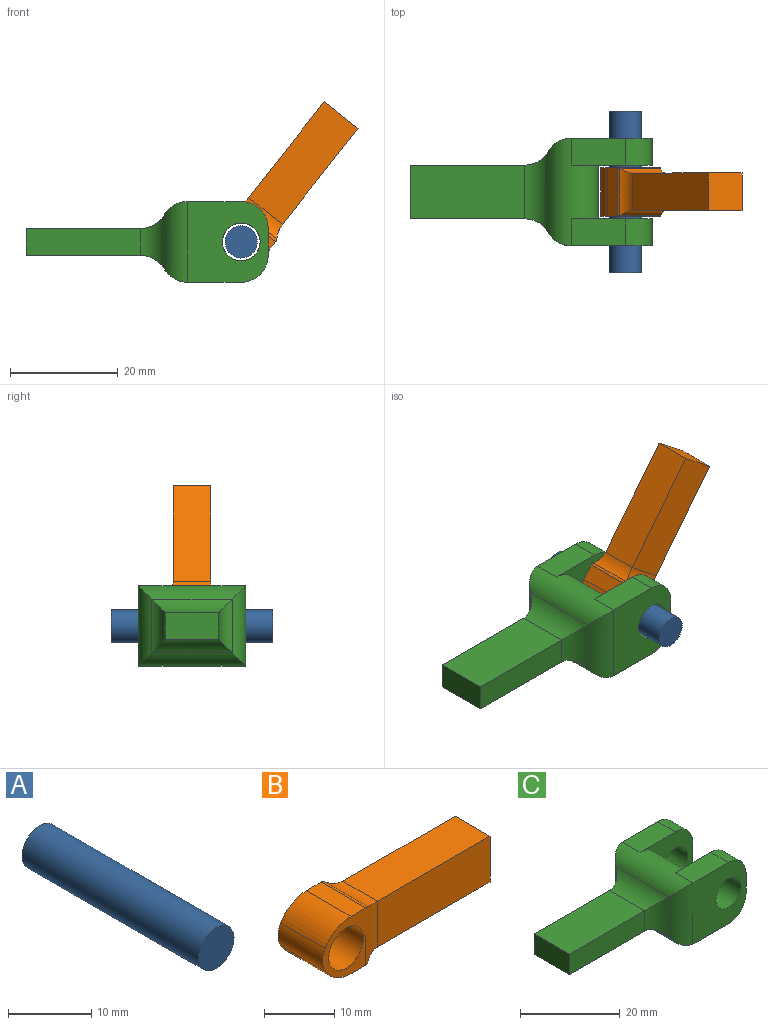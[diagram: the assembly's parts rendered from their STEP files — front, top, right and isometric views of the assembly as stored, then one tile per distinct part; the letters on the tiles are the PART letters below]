
ASSEMBLY  parts=3 mates=2
PART A: 3 faces, bbox 6x30x6 mm
  f0: cylinder r=3mm len=30mm, axis (0,1,0), area 565.5mm2, adj f1,f2
  f1: plane 6x6mm, normal (0,-1,0), area 28.3mm2, adj f0
  f2: plane 6x6mm, normal (0,1,0), area 28.3mm2, adj f0
PART B: 21 faces, bbox 34.7x9x10 mm
  f0: plane 10x8.73mm, normal (0,1,0), area 35.9mm2, adj f2,f3,f4,f5,f6,f10,f20
  f1: plane 10x8.73mm, normal (0,-1,0), area 35.9mm2, adj f2,f3,f4,f5,f6,f7,f20
  f2: plane 9x3mm, normal (0,0,1), area 27mm2, adj f0,f1,f5,f8
  f3: plane 9x3mm, normal (0,0,-1), area 27mm2, adj f0,f1,f6,f9
  f4: cylinder r=3.5mm len=9mm, axis (0,1,0), area 197.9mm2, adj f0,f1
  f5: cylinder r=6mm len=9mm, axis (0,1,0), area 56.5mm2, adj f0,f1,f2,f20
  f6: cylinder r=6mm len=9mm, axis (0,-1,0), area 56.5mm2, adj f0,f1,f3,f20
  f7: cylinder r=1mm len=10mm, axis (0,0,1), area 5.8mm2, adj f1,f8,f9,f17
  f8: cylinder r=1mm len=9mm, axis (0,-1,0), area 5.2mm2, adj f2,f7,f10,f16
  f9: cylinder r=1mm len=9mm, axis (0,1,0), area 5.2mm2, adj f3,f7,f10,f19
  f10: cylinder r=1mm len=10mm, axis (0,0,-1), area 5.8mm2, adj f0,f8,f9,f18
  f11: plane 22.68x7mm, normal (0,0,1), area 158.8mm2, adj f12,f14,f15,f16
  f12: plane 22.68x8mm, normal (0,-1,0), area 181.5mm2, adj f11,f13,f15,f17
  f13: plane 22.68x7mm, normal (0,0,-1), area 158.8mm2, adj f12,f14,f15,f19
  f14: plane 22.68x8mm, normal (0,1,0), area 181.5mm2, adj f11,f13,f15,f18
  f15: plane 8x7mm, normal (1,0,0), area 56mm2, adj f11,f12,f13,f14
  f16: cylinder r=5mm len=8.67mm, axis (0,-1,0), area 22.1mm2, adj f8,f11,f17,f18
  f17: cylinder r=5mm len=9.67mm, axis (0,0,1), area 25.1mm2, adj f7,f12,f16,f19
  f18: cylinder r=5mm len=9.67mm, axis (0,0,-1), area 25.1mm2, adj f10,f14,f16,f19
  f19: cylinder r=5mm len=8.67mm, axis (0,1,0), area 22.1mm2, adj f9,f13,f17,f18
  f20: cylinder r=4mm len=9mm, axis (0,1,0), area 37.7mm2, adj f0,f1,f5,f6
PART C: 30 faces, bbox 45x20x15 mm
  f0: plane 10x5mm, normal (0,0,1), area 50mm2, adj f5,f7,f14,f19
  f1: plane 10x5mm, normal (0,0,-1), area 50mm2, adj f5,f7,f15,f17
  f2: plane 5x5mm, normal (1,0,0), area 25mm2, adj f3,f8,f18,f20
  f3: plane 15x15mm, normal (0,1,0), area 111.5mm2, adj f2,f4,f9,f10,f11,f14,f15,f18
  f4: plane 10x5mm, normal (1,0,0), area 50mm2, adj f3,f5,f14,f15
  f5: plane 15x15mm, normal (0,-1,0), area 111.5mm2, adj f0,f1,f4,f6,f12,f14,f15,f17
  f6: plane 5x5mm, normal (1,0,0), area 25mm2, adj f5,f7,f17,f19
  f7: plane 15x15mm, normal (0,1,0), area 175.8mm2, adj f0,f1,f6,f12,f16,f17,f19
  f8: plane 15x15mm, normal (0,-1,0), area 175.8mm2, adj f2,f9,f10,f11,f13,f18,f20
  f9: plane 10x5mm, normal (0,0,1), area 50mm2, adj f3,f8,f14,f20
  f10: plane 10x5mm, normal (0,0,-1), area 50mm2, adj f3,f8,f15,f18
  f11: cylinder r=3.5mm len=7mm, axis (0,1,0), area 110mm2, adj f3,f8
  f12: cylinder r=3.5mm len=7mm, axis (0,1,0), area 110mm2, adj f5,f7
  f13: cylinder r=5mm len=15mm, axis (0,0,-1), area 69.5mm2, adj f8,f14,f15,f28
  f14: cylinder r=5mm len=20mm, axis (0,1,0), area 174.2mm2, adj f0,f3,f4,f5,f9,f13,f16,f26
  f15: cylinder r=5mm len=20mm, axis (0,-1,0), area 174.2mm2, adj f1,f3,f4,f5,f10,f13,f16,f29
  f16: cylinder r=5mm len=15mm, axis (0,0,1), area 69.5mm2, adj f7,f14,f15,f27
  f17: cylinder r=5mm len=5mm, axis (0,1,0), area 39.3mm2, adj f1,f5,f6,f7
  f18: cylinder r=5mm len=5mm, axis (0,1,0), area 39.3mm2, adj f2,f3,f8,f10
  f19: cylinder r=5mm len=5mm, axis (0,-1,0), area 39.3mm2, adj f0,f5,f6,f7
  f20: cylinder r=5mm len=5mm, axis (0,-1,0), area 39.3mm2, adj f2,f3,f8,f9
  f21: plane 21.34x10mm, normal (0,0,1), area 213.4mm2, adj f22,f24,f25,f26
  f22: plane 21.34x5mm, normal (0,1,0), area 106.7mm2, adj f21,f23,f25,f27
  f23: plane 21.34x10mm, normal (0,0,-1), area 213.4mm2, adj f22,f24,f25,f29
  f24: plane 21.34x5mm, normal (0,-1,0), area 106.7mm2, adj f21,f23,f25,f28
  f25: plane 10x5mm, normal (-1,0,0), area 50mm2, adj f21,f22,f23,f24
  f26: cylinder r=5mm len=15mm, axis (0,1,0), area 61.4mm2, adj f14,f21,f27,f28
  f27: cylinder r=5mm len=10mm, axis (0,0,1), area 35.2mm2, adj f16,f22,f26,f29
  f28: cylinder r=5mm len=10mm, axis (0,0,-1), area 35.2mm2, adj f13,f24,f26,f29
  f29: cylinder r=5mm len=15mm, axis (0,-1,0), area 61.4mm2, adj f15,f23,f27,f28
PLACE A t=(2.79,-1.27,0.01)mm
PLACE B rot(axis=(0,-1,0),51.8deg) t=(2.79,-1.27,0.01)mm
PLACE C t=(-2.21,-1.27,0.01)mm fixed
MATE fastened A.f0 <-> C.f11  axis (0,1,0) through (2.79,-1.27,0.01)mm
MATE revolute A.f0 <-> B.f4  axis (0,1,0) through (2.79,-1.27,0.01)mm
